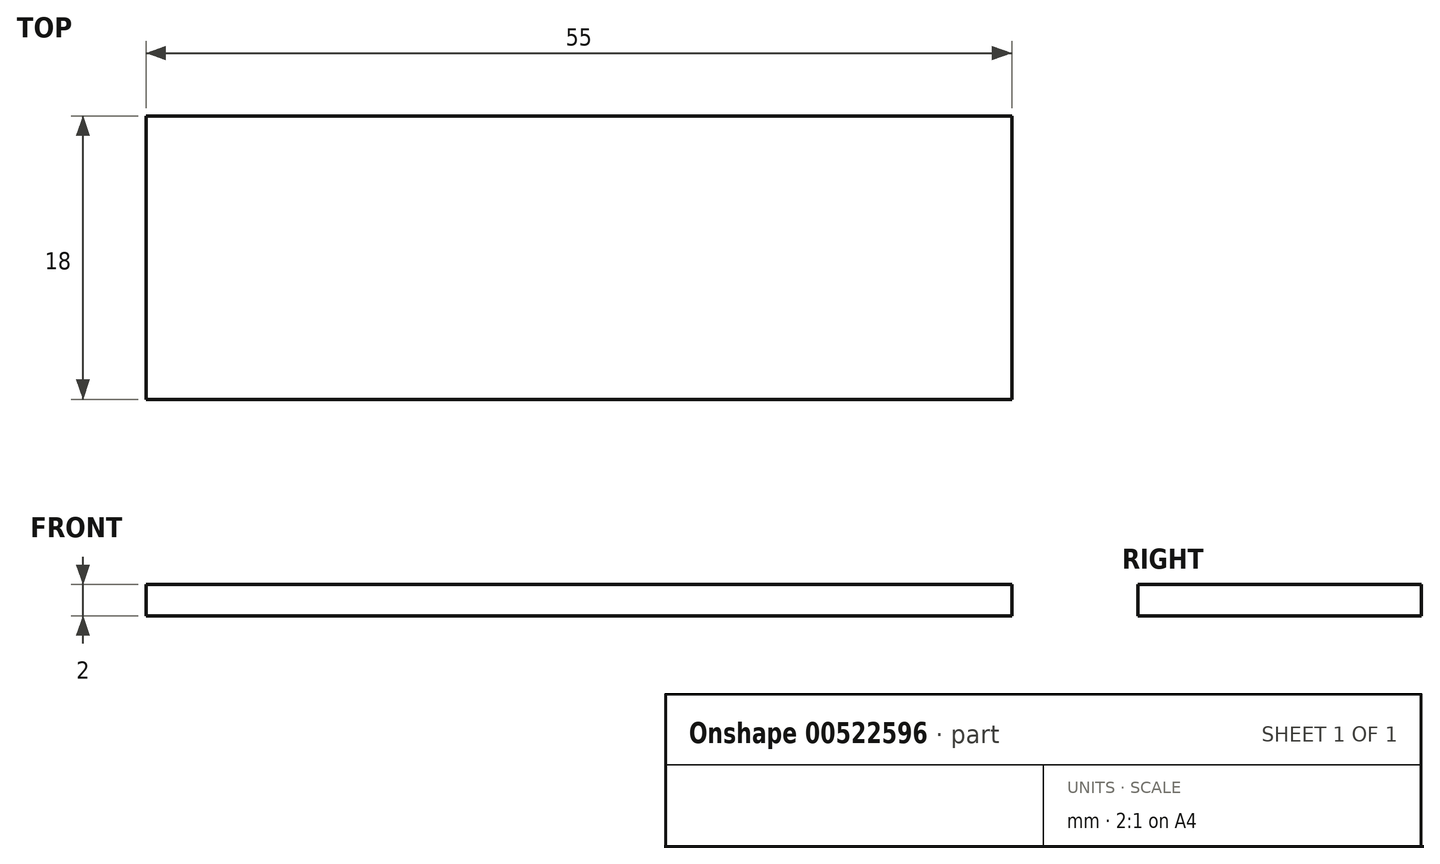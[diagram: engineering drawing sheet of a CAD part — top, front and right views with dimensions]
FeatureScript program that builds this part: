
annotation { "Feature Type Name" : "Feature", "Feature Type Description" : "" }
export const myFeature = defineFeature(function(context is Context, id is Id, definition is map)
    precondition{}
    {
        {
            var Q0;
            Q0=qCreatedBy(makeId("Top.planeOp"),FACE);
            var sketch = newSketch(context, id + "F0", { "sketchPlane" : qUnion([Q0])});
            skLineSegment(sketch, "E0.bottom", {"start": v(-27.5, 9) * mm, "end": v(27.5, 9) * mm});
            skLineSegment(sketch, "E0.top", {"start": v(-27.5, -9) * mm, "end": v(27.5, -9) * mm});
            skLineSegment(sketch, "E0.left", {"start": v(-27.5, 9) * mm, "end": v(-27.5, -9) * mm});
            skLineSegment(sketch, "E0.right", {"start": v(27.5, 9) * mm, "end": v(27.5, -9) * mm});
            skPoint(sketch, "E0.middle", {"position": v(0, 0) * mm});
            skSolve(sketch);
        }
        {
            var Q0;
            Q0=makeQuery(id+"F0.imprint","IMPRINT",FACE,{"disambiguationData":[TD([[makeQuery(id+"F0.imprint","IMPRINT",EDGE,{"derivedFrom":sQuery(id+"F0.wireOp",EDGE,"E0.bottom")}),-1.0]])]});
            extrude(context, id + "F1", {"entities" : qUnion([Q0]), "depth" : 2 * mm, "offsetDistance" : 25 * mm});
        }
        {
            var Q0;
            Q0=qCreatedBy(makeId("Top.planeOp"),FACE);
            var sketch = newSketch(context, id + "F2", { "sketchPlane" : qUnion([Q0])});
            skLineSegment(sketch, "E1.bottom", {"start": v(-27.5, 9) * mm, "end": v(27.5, 9) * mm});
            skLineSegment(sketch, "E1.top", {"start": v(-27.5, -9) * mm, "end": v(27.5, -9) * mm});
            skLineSegment(sketch, "E1.left", {"start": v(-27.5, 9) * mm, "end": v(-27.5, -9) * mm});
            skLineSegment(sketch, "E1.right", {"start": v(27.5, 9) * mm, "end": v(27.5, -9) * mm});
            skPoint(sketch, "E1.middle", {"position": v(0, 0) * mm});
            skSolve(sketch);
        }
        {
            var Q0;
            Q0 = qSketchRegion(id + "F2", true);
            extrude(context, id + "F3", {"entities" : qUnion([Q0]), "operationType" : NewBodyOperationType.ADD, "depth" : 2 * mm, "offsetDistance" : 25 * mm});
        }
    });
